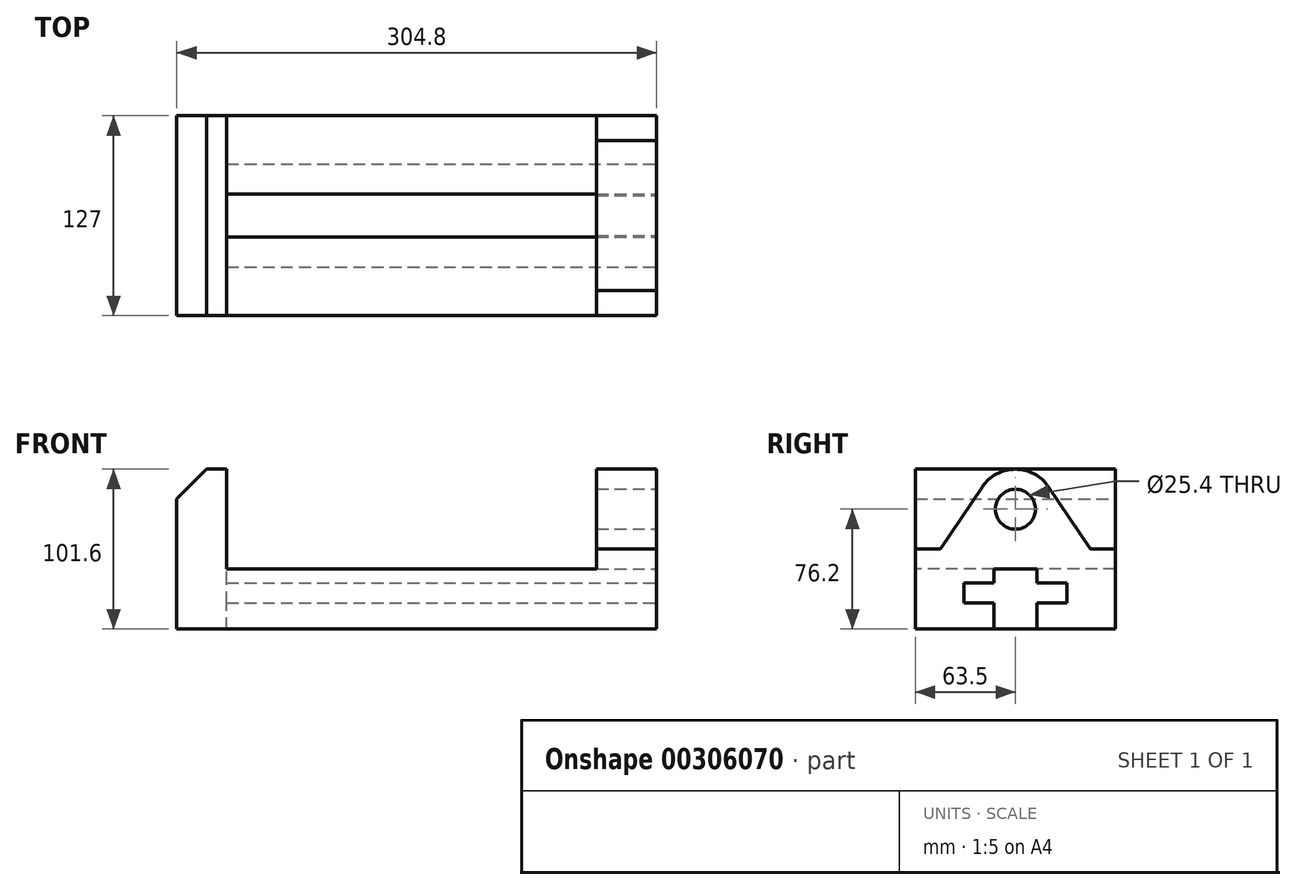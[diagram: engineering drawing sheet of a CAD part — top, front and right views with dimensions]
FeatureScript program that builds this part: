
annotation { "Feature Type Name" : "Feature", "Feature Type Description" : "" }
export const myFeature = defineFeature(function(context is Context, id is Id, definition is map)
    precondition{}
    {
        {
            var Q0;
            Q0=qCreatedBy(makeId("Front.planeOp"),FACE);
            var sketch = newSketch(context, id + "F0", { "sketchPlane" : qUnion([Q0])});
            skLineSegment(sketch, "E0", {"start": v(0, 0) * mm, "end": v(304.8, 0) * mm});
            skLineSegment(sketch, "E1", {"start": v(304.8, 0) * mm, "end": v(304.8, 101.6) * mm});
            skLineSegment(sketch, "E2", {"start": v(304.8, 101.6) * mm, "end": v(0, 101.6) * mm});
            skLineSegment(sketch, "E3", {"start": v(0, 101.6) * mm, "end": v(0, 0) * mm});
            skSolve(sketch);
        }
        {
            var Q0;
            Q0=makeQuery(id+"F0.imprint","IMPRINT",FACE,{"disambiguationData":[TD([[makeQuery(id+"F0.imprint","IMPRINT",EDGE,{"derivedFrom":sQuery(id+"F0.wireOp",EDGE,"E0")}),1.0]])]});
            extrude(context, id + "F1", {"entities" : qUnion([Q0]), "endBound" : BoundingType.SYMMETRIC, "depth" : 127 * mm});
        }
        {
            var Q0;
            Q0=makeQuery(id+"F1.opExtrude","CAP_FACE",FACE,{"disambiguationData":[OSD([sQuery(id+"F0.wireOp",EDGE,"E0"),sQuery(id+"F0.wireOp",EDGE,"E1"),sQuery(id+"F0.wireOp",EDGE,"E2"),sQuery(id+"F0.wireOp",EDGE,"E3")])],"isStart":false});
            var sketch = newSketch(context, id + "F2", { "sketchPlane" : qUnion([Q0])});
            skLineSegment(sketch, "E4", {"start": v(31.75, 101.6) * mm, "end": v(266.7, 101.6) * mm});
            skLineSegment(sketch, "E5", {"start": v(31.75, 101.6) * mm, "end": v(31.75, 38.1) * mm});
            skLineSegment(sketch, "E6", {"start": v(31.75, 38.1) * mm, "end": v(266.7, 38.1) * mm});
            skLineSegment(sketch, "E7", {"start": v(266.7, 38.1) * mm, "end": v(266.7, 101.6) * mm});
            skSolve(sketch);
        }
        {
            var Q0;
            Q0 = qSketchRegion(id + "F2", true);
            extrude(context, id + "F3", {"entities" : qUnion([Q0]), "operationType" : NewBodyOperationType.REMOVE, "endBound" : BoundingType.THROUGH_ALL, "oppositeDirection" : true, "depth" : 25.4 * mm});
        }
        {
            var Q0;
            Q0=makeQuery(id+"F1.opExtrude","SWEPT_EDGE",EDGE,{"disambiguationData":[OSD([sQuery(id+"F0.wireOp",EDGE,"E2"),sQuery(id+"F0.wireOp",EDGE,"E3")])]});
            chamfer(context, id + "F4", {"entities" : qUnion([Q0]), "chamferType" : ChamferType.TWO_OFFSETS, "width1" : 19.05 * mm, "oppositeDirection" : false, "width2" : 19.05 * mm, "tangentPropagation" : true});
        }
        {
            var Q0;
            Q0=makeQuery(id+"F1.opExtrude","SWEPT_FACE",FACE,{"disambiguationData":[OSD([sQuery(id+"F0.wireOp",EDGE,"E1")])]});
            var sketch = newSketch(context, id + "F5", { "sketchPlane" : qUnion([Q0])});
            skLineSegment(sketch, "E8", {"start": v(-63.5, 50.8) * mm, "end": v(-47.63, 50.8) * mm});
            skLineSegment(sketch, "E9", {"start": v(47.63, 50.8) * mm, "end": v(63.5, 50.8) * mm});
            skLineSegment(sketch, "E10", {"start": v(-47.63, 50.8) * mm, "end": v(-21.1, 90.35) * mm});
            skLineSegment(sketch, "E11", {"start": v(47.63, 50.8) * mm, "end": v(21.1, 90.35) * mm});
            skCircle(sketch, "E12", {"center": v(0, 76.2) * mm, "radius": 12.7 * mm});
            skArc(sketch, "E13", {"start": v(-21.1, 90.35) * mm, "mid": v(0, 101.6) * mm, "end": v(21.1, 90.35) * mm});
            skLineSegment(sketch, "E14", {"start": v(-63.5, 50.8) * mm, "end": v(-63.5, 101.6) * mm});
            skLineSegment(sketch, "E15", {"start": v(-63.5, 101.6) * mm, "end": v(63.5, 101.6) * mm});
            skLineSegment(sketch, "E16", {"start": v(63.5, 101.6) * mm, "end": v(63.5, 50.8) * mm});
            skSolve(sketch);
        }
        {
            var Q0;
            Q0 = qSketchRegion(id + "F5", true);
            extrude(context, id + "F6", {"entities" : qUnion([Q0]), "operationType" : NewBodyOperationType.REMOVE, "oppositeDirection" : true, "depth" : 38.1 * mm});
        }
        {
            var Q0;
            Q0=makeQuery(id+"F1.opExtrude","SWEPT_FACE",FACE,{"disambiguationData":[OSD([sQuery(id+"F0.wireOp",EDGE,"E1")])]});
            var sketch = newSketch(context, id + "F7", { "sketchPlane" : qUnion([Q0])});
            skLineSegment(sketch, "E17", {"start": v(0, -21.64) * mm, "end": v(0, 114.52) * mm, "construction": true});
            skPoint(sketch, "E17.startSnap0", {"position": v(0, 0) * mm});
            skLineSegment(sketch, "E18", {"start": v(0, 0) * mm, "end": v(-13.68, 0) * mm});
            skLineSegment(sketch, "E19", {"start": v(-13.68, 0) * mm, "end": v(-13.68, 16.5) * mm});
            skLineSegment(sketch, "E20", {"start": v(-13.68, 16.5) * mm, "end": v(-32.73, 16.5) * mm});
            skLineSegment(sketch, "E21", {"start": v(-32.73, 16.5) * mm, "end": v(-32.73, 29.2) * mm});
            skLineSegment(sketch, "E22", {"start": v(-32.73, 29.2) * mm, "end": v(-13.68, 29.2) * mm});
            skLineSegment(sketch, "E23", {"start": v(-13.68, 29.2) * mm, "end": v(-13.68, 38.1) * mm});
            skLineSegment(sketch, "E24", {"start": v(-13.68, 38.1) * mm, "end": v(0, 38.1) * mm});
            skLineSegment(sketch, "E25.MirrorCS", {"start": v(13.68, 38.1) * mm, "end": v(0, 38.1) * mm});
            skLineSegment(sketch, "E26.MirrorCS", {"start": v(13.68, 29.2) * mm, "end": v(13.68, 38.1) * mm});
            skLineSegment(sketch, "E27.MirrorCS", {"start": v(32.73, 29.2) * mm, "end": v(13.68, 29.2) * mm});
            skLineSegment(sketch, "E28.MirrorCS", {"start": v(13.68, 16.5) * mm, "end": v(32.73, 16.5) * mm});
            skLineSegment(sketch, "E29.MirrorCS", {"start": v(32.73, 16.5) * mm, "end": v(32.73, 29.2) * mm});
            skLineSegment(sketch, "E30.MirrorCS", {"start": v(13.68, 0) * mm, "end": v(13.68, 16.5) * mm});
            skLineSegment(sketch, "E31.MirrorCS", {"start": v(0, 0) * mm, "end": v(13.68, 0) * mm});
            skSolve(sketch);
        }
        {
            var Q0;
            Q0=makeQuery(id+"F7.imprint","IMPRINT",FACE,{"disambiguationData":[TD([[makeQuery(id+"F7.imprint","IMPRINT",EDGE,{"derivedFrom":sQuery(id+"F7.wireOp",EDGE,"E18")}),1.0]])]});
            extrude(context, id + "F8", {"entities" : qUnion([Q0]), "operationType" : NewBodyOperationType.REMOVE, "oppositeDirection" : true, "depth" : 273.05 * mm});
        }
    });
